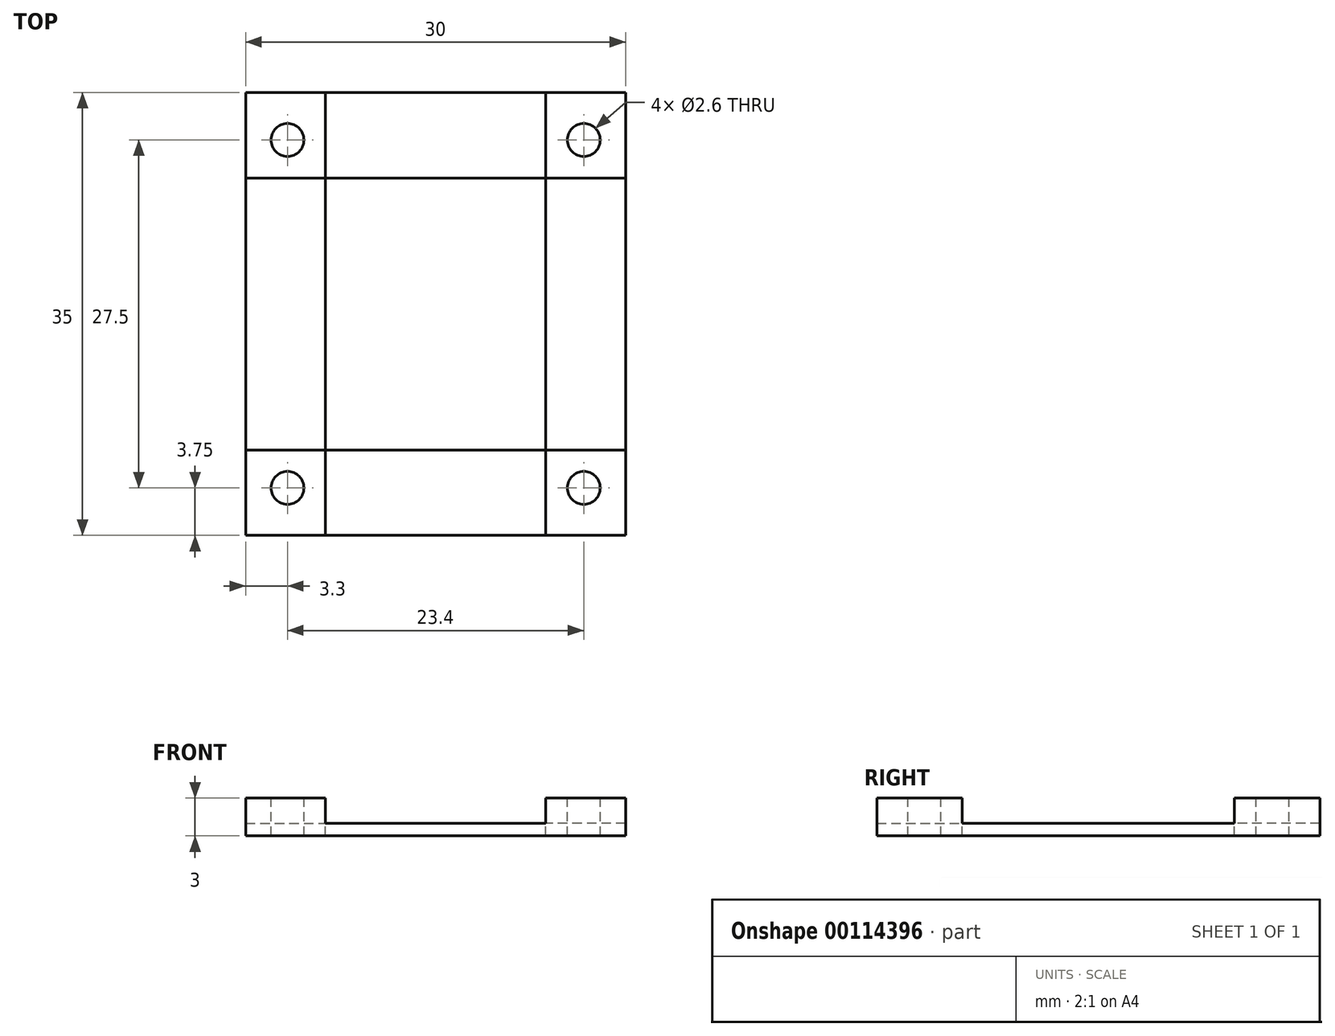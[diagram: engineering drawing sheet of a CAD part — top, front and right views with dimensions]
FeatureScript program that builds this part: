
annotation { "Feature Type Name" : "Feature", "Feature Type Description" : "" }
export const myFeature = defineFeature(function(context is Context, id is Id, definition is map)
    precondition{}
    {
        {
            var Q0;
            Q0=qCreatedBy(makeId("Top.planeOp"),FACE);
            var sketch = newSketch(context, id + "F0", { "sketchPlane" : qUnion([Q0])});
            skLineSegment(sketch, "E0.bottom", {"start": v(0, 0) * mm, "end": v(23.4, 0) * mm, "construction": true});
            skLineSegment(sketch, "E0.top", {"start": v(0, 27.5) * mm, "end": v(23.4, 27.5) * mm, "construction": true});
            skLineSegment(sketch, "E0.left", {"start": v(0, 0) * mm, "end": v(0, 27.5) * mm, "construction": true});
            skLineSegment(sketch, "E0.right", {"start": v(23.4, 0) * mm, "end": v(23.4, 27.5) * mm, "construction": true});
            skCircle(sketch, "E1", {"center": v(0, 27.5) * mm, "radius": 1.3 * mm, "construction": true});
            skCircle(sketch, "E2", {"center": v(0, 0) * mm, "radius": 1.3 * mm, "construction": true});
            skCircle(sketch, "E3", {"center": v(23.4, 0) * mm, "radius": 1.3 * mm, "construction": true});
            skCircle(sketch, "E4", {"center": v(23.4, 27.5) * mm, "radius": 1.3 * mm, "construction": true});
            skLineSegment(sketch, "E5", {"start": v(11.7, 27.5) * mm, "end": v(11.7, 0) * mm, "construction": true});
            skLineSegment(sketch, "E6", {"start": v(0, 13.75) * mm, "end": v(23.4, 13.75) * mm, "construction": true});
            skSolve(sketch);
        }
        {
            var Q0;
            Q0=qCreatedBy(makeId("Top.planeOp"),FACE);
            var sketch = newSketch(context, id + "F1", { "sketchPlane" : qUnion([Q0])});
            skLineSegment(sketch, "E7.bottom", {"start": v(-3.3, -3.75) * mm, "end": v(26.7, -3.75) * mm});
            skLineSegment(sketch, "E7.top", {"start": v(-3.3, 31.25) * mm, "end": v(26.7, 31.25) * mm});
            skLineSegment(sketch, "E7.left", {"start": v(-3.3, -3.75) * mm, "end": v(-3.3, 31.25) * mm});
            skLineSegment(sketch, "E7.right", {"start": v(26.7, -3.75) * mm, "end": v(26.7, 31.25) * mm});
            skLineSegment(sketch, "E8", {"start": v(11.7, 27.5) * mm, "end": v(11.7, 31.25) * mm, "construction": true});
            skLineSegment(sketch, "E9", {"start": v(-3.3, 13.75) * mm, "end": v(0, 13.75) * mm, "construction": true});
            skSolve(sketch);
        }
        {
            var Q0;
            Q0 = qSketchRegion(id + "F1", true);
            extrude(context, id + "F2", {"entities" : qUnion([Q0]), "depth" : 1 * mm});
        }
        {
            var Q0;
            Q0=makeQuery(id+"F2.opExtrude","CAP_FACE",FACE,{"disambiguationData":[OSD([sQuery(id+"F1.wireOp",EDGE,"E7.bottom"),sQuery(id+"F1.wireOp",EDGE,"E7.top"),sQuery(id+"F1.wireOp",EDGE,"E7.left"),sQuery(id+"F1.wireOp",EDGE,"E7.right")])],"isStart":false});
            var sketch = newSketch(context, id + "F3", { "sketchPlane" : qUnion([Q0])});
            skLineSegment(sketch, "E10.bottom", {"start": v(-3.3, 31.25) * mm, "end": v(3, 31.25) * mm});
            skLineSegment(sketch, "E10.top", {"start": v(-3.3, 24.5) * mm, "end": v(3, 24.5) * mm});
            skLineSegment(sketch, "E10.left", {"start": v(-3.3, 31.25) * mm, "end": v(-3.3, 24.5) * mm});
            skLineSegment(sketch, "E10.right", {"start": v(3, 31.25) * mm, "end": v(3, 24.5) * mm});
            skLineSegment(sketch, "E11", {"start": v(11.7, 31.25) * mm, "end": v(11.7, -3.75) * mm, "construction": true});
            skLineSegment(sketch, "E12", {"start": v(-3.3, 13.75) * mm, "end": v(26.7, 13.75) * mm, "construction": true});
            skLineSegment(sketch, "E13.MirrorCS", {"start": v(26.7, 31.25) * mm, "end": v(20.4, 31.25) * mm});
            skLineSegment(sketch, "E14.MirrorCS", {"start": v(26.7, 24.5) * mm, "end": v(20.4, 24.5) * mm});
            skLineSegment(sketch, "E15.MirrorCS", {"start": v(26.7, 31.25) * mm, "end": v(26.7, 24.5) * mm});
            skLineSegment(sketch, "E16.MirrorCS", {"start": v(20.4, 31.25) * mm, "end": v(20.4, 24.5) * mm});
            skLineSegment(sketch, "E17.MirrorCS", {"start": v(20.4, -3.75) * mm, "end": v(20.4, 3) * mm});
            skLineSegment(sketch, "E18.MirrorCS", {"start": v(26.7, -3.75) * mm, "end": v(26.7, 3) * mm});
            skLineSegment(sketch, "E19.MirrorCS", {"start": v(26.7, 3) * mm, "end": v(20.4, 3) * mm});
            skLineSegment(sketch, "E20.MirrorCS", {"start": v(26.7, -3.75) * mm, "end": v(20.4, -3.75) * mm});
            skLineSegment(sketch, "E21.MirrorCS", {"start": v(-3.3, 3) * mm, "end": v(3, 3) * mm});
            skLineSegment(sketch, "E22.MirrorCS", {"start": v(-3.3, -3.75) * mm, "end": v(-3.3, 3) * mm});
            skLineSegment(sketch, "E23.MirrorCS", {"start": v(-3.3, -3.75) * mm, "end": v(3, -3.75) * mm});
            skLineSegment(sketch, "E24.MirrorCS", {"start": v(3, -3.75) * mm, "end": v(3, 3) * mm});
            skSolve(sketch);
        }
        {
            var Q0;
            Q0 = qSketchRegion(id + "F3", true);
            extrude(context, id + "F4", {"entities" : qUnion([Q0]), "operationType" : NewBodyOperationType.ADD, "depth" : 2 * mm});
        }
        {
            var Q0;
            Q0=makeQuery(id+"F4.opExtrude","CAP_FACE",FACE,{"disambiguationData":[OSD([sQuery(id+"F3.wireOp",EDGE,"E10.bottom"),sQuery(id+"F3.wireOp",EDGE,"E10.top"),sQuery(id+"F3.wireOp",EDGE,"E10.left"),sQuery(id+"F3.wireOp",EDGE,"E10.right")])],"isStart":false});
            var sketch = newSketch(context, id + "F5", { "sketchPlane" : qUnion([Q0])});
            skCircle(sketch, "E25.0", {"center": v(0, 27.5) * mm, "radius": 1.3 * mm});
            skCircle(sketch, "E26.0", {"center": v(23.4, 27.5) * mm, "radius": 1.3 * mm});
            skCircle(sketch, "E27.0", {"center": v(23.4, 0) * mm, "radius": 1.3 * mm});
            skCircle(sketch, "E27.1", {"center": v(0, 0) * mm, "radius": 1.3 * mm});
            skSolve(sketch);
        }
        {
            var Q0;
            Q0 = qSketchRegion(id + "F5", true);
            extrude(context, id + "F6", {"entities" : qUnion([Q0]), "operationType" : NewBodyOperationType.REMOVE, "endBound" : BoundingType.THROUGH_ALL, "oppositeDirection" : true, "depth" : 25 * mm});
        }
        {
            var Q0;
            Q0=makeQuery(id+"F2.opExtrude","CAP_FACE",FACE,{"disambiguationData":[OSD([sQuery(id+"F1.wireOp",EDGE,"E7.bottom"),sQuery(id+"F1.wireOp",EDGE,"E7.top"),sQuery(id+"F1.wireOp",EDGE,"E7.left"),sQuery(id+"F1.wireOp",EDGE,"E7.right")])],"isStart":false});
            var sketch = newSketch(context, id + "F7", { "sketchPlane" : qUnion([Q0])});
            skLineSegment(sketch, "E28.bottom", {"start": v(3, 24.5) * mm, "end": v(20.4, 24.5) * mm});
            skLineSegment(sketch, "E28.top", {"start": v(3, 3) * mm, "end": v(20.4, 3) * mm});
            skLineSegment(sketch, "E28.left", {"start": v(3, 24.5) * mm, "end": v(3, 3) * mm});
            skLineSegment(sketch, "E28.right", {"start": v(20.4, 24.5) * mm, "end": v(20.4, 3) * mm});
            skLineSegment(sketch, "E29.0", {"start": v(26.7, 24.5) * mm, "end": v(20.4, 24.5) * mm, "construction": true});
            skLineSegment(sketch, "E30.0", {"start": v(-3.3, 24.5) * mm, "end": v(3, 24.5) * mm, "construction": true});
            skLineSegment(sketch, "E31.0", {"start": v(26.7, 3) * mm, "end": v(20.4, 3) * mm, "construction": true});
            skLineSegment(sketch, "E32.0", {"start": v(-3.3, 3) * mm, "end": v(3, 3) * mm, "construction": true});
            skSolve(sketch);
        }
        {
            var Q0;
            Q0=makeQuery(id+"F7.imprint","IMPRINT",FACE,{"disambiguationData":[TD([[makeQuery(id+"F7.imprint","IMPRINT",EDGE,{"derivedFrom":sQuery(id+"F7.wireOp",EDGE,"E28.bottom")}),-1.0]])]});
            extrude(context, id + "F8", {"entities" : qUnion([Q0]), "operationType" : NewBodyOperationType.REMOVE, "endBound" : BoundingType.THROUGH_ALL, "oppositeDirection" : true, "depth" : 25 * mm});
        }
    });
